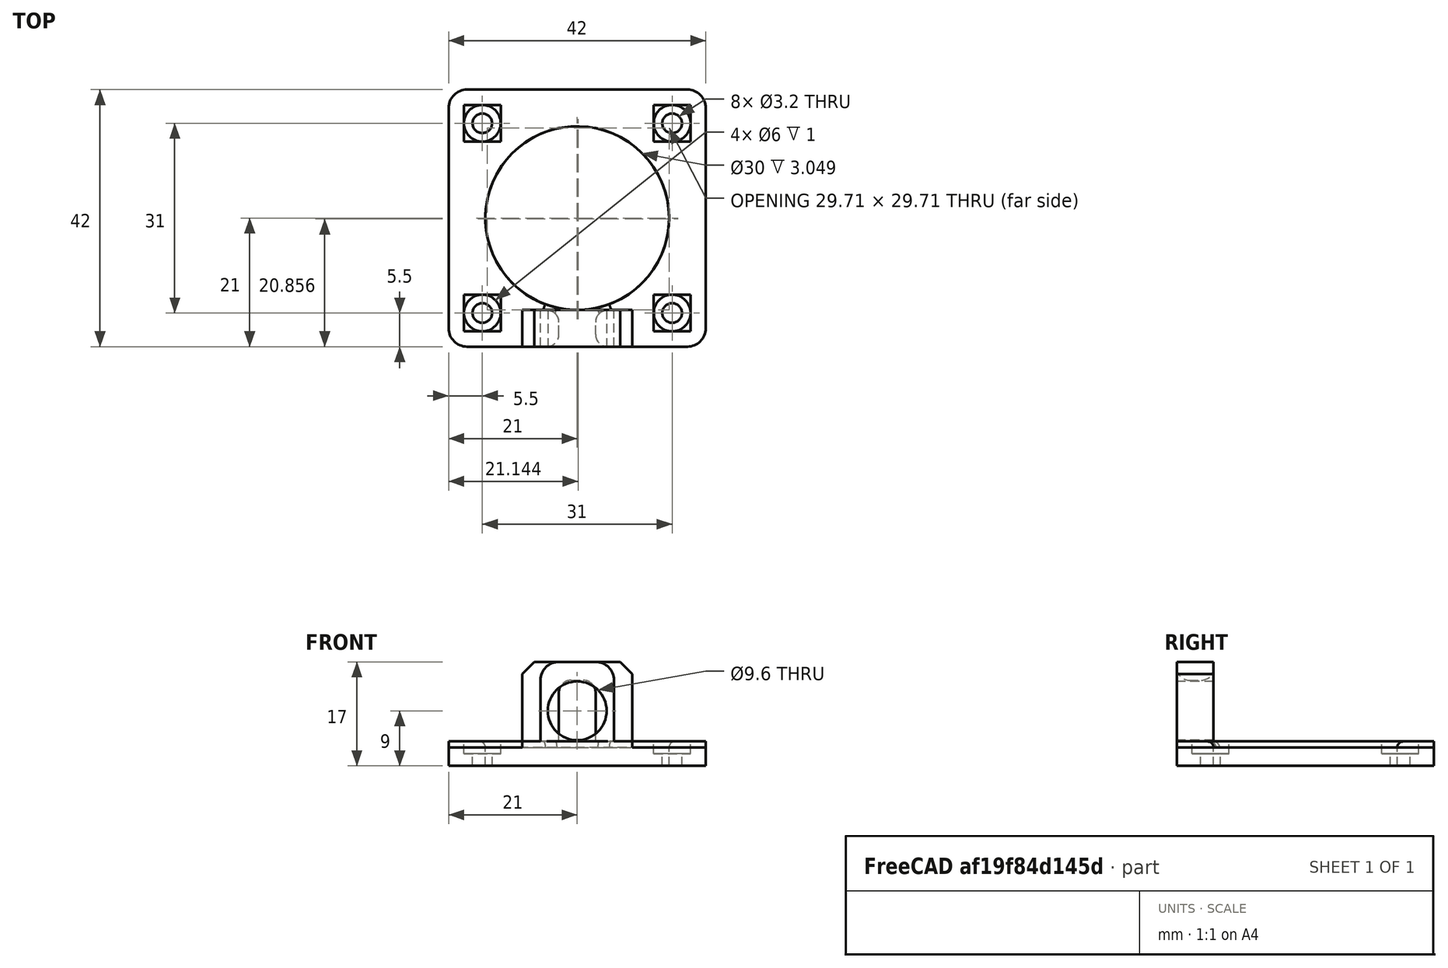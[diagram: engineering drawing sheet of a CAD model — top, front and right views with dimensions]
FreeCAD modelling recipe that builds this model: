
FCSTD DOCUMENT  (FreeCAD 0.18R14555 (Git shallow))
Label: tube-mounter
License: All rights reserved
LicenseURL: http://en.wikipedia.org/wiki/All_rights_reserved
objects: Part::Cylinder×15, Part::Box×9, Part::Cut×8, Part::MultiFuse×6, Part::Fillet×5, Part::Chamfer×1
note: 44 computed .brp shape members not serialized (recipe doc carries the construction recipe); baked Part::Feature solids carry a one-line shape summary decoded from their .brp

FEATURE [Part::Box] Box  label="Cube"
  AttacherType = Attacher::AttachEngine3D
  Height = 3
  Length = 42
  Width = 42
FEATURE [Part::Cylinder] Cylinder
  Angle = 360
  AttacherType = Attacher::AttachEngine3D
  Height = 3
  Placement = pos=(5.5,5.5,0) rot=(0,0,1;0rad)
  Radius = 1.6
FEATURE [Part::Cylinder] Cylinder001
  Angle = 360
  AttacherType = Attacher::AttachEngine3D
  Height = 3
  Placement = pos=(36.5,5.5,0) rot=(0,0,1;0rad)
  Radius = 1.6
FEATURE [Part::Cylinder] Cylinder002
  Angle = 360
  AttacherType = Attacher::AttachEngine3D
  Height = 3
  Placement = pos=(5.5,36.5,0) rot=(0,0,1;0rad)
  Radius = 1.6
FEATURE [Part::Cylinder] Cylinder003
  Angle = 360
  AttacherType = Attacher::AttachEngine3D
  Height = 3
  Placement = pos=(36.5,36.5,0) rot=(0,0,1;0rad)
  Radius = 1.6
FEATURE [Part::Box] Box001  label="Cube001"
  AttacherType = Attacher::AttachEngine3D
  Height = 2
  Length = 6
  Placement = pos=(2.5,2.5,1) rot=(0,0,1;0rad)
  Width = 6
FEATURE [Part::Cylinder] Cylinder004
  Angle = 360
  AttacherType = Attacher::AttachEngine3D
  Height = 1
  Placement = pos=(36.5,36.5,0) rot=(0,0,1;0rad)
  Radius = 3
FEATURE [Part::Cylinder] Cylinder005
  Angle = 360
  AttacherType = Attacher::AttachEngine3D
  Height = 1
  Placement = pos=(5.5,5.5,0) rot=(0,0,1;0rad)
  Radius = 3
FEATURE [Part::Cylinder] Cylinder006
  Angle = 360
  AttacherType = Attacher::AttachEngine3D
  Height = 1
  Placement = pos=(36.5,5.5,0) rot=(0,0,1;0rad)
  Radius = 3
FEATURE [Part::Cylinder] Cylinder007
  Angle = 360
  AttacherType = Attacher::AttachEngine3D
  Height = 1
  Placement = pos=(5.5,36.5,0) rot=(0,0,1;0rad)
  Radius = 3
FEATURE [Part::MultiFuse] Fusion
  Shapes = -> [Cylinder003,Cylinder,Cylinder001,Cylinder002]
FEATURE [Part::MultiFuse] Fusion001
  Placement = pos=(0,0,2) rot=(0,0,1;0rad)
  Shapes = -> [Cylinder004,Cylinder007,Cylinder006,Cylinder005]
FEATURE [Part::Box] Box002  label="Cube002"
  AttacherType = Attacher::AttachEngine3D
  Height = 4
  Length = 42
  Width = 42
FEATURE [Part::Cut] Cut
  Base = -> Box
  Tool = -> Fusion
FEATURE [Part::Cut] Cut001
  Base = -> Cut
  Tool = -> Fusion001
FEATURE [Part::Fillet] Fillet
  Base = -> Cut001
  Edges = 4 edges r=3: [Edge1,Edge3,Edge6,Edge15]
FEATURE [Part::Cylinder] Cylinder008
  Angle = 360
  AttacherType = Attacher::AttachEngine3D
  Height = 3
  Placement = pos=(21,21,0) rot=(0,0,1;0rad)
  Radius = 15
FEATURE [Part::Cut] Cut002
  Base = -> Fillet
  Tool = -> Cylinder008
FEATURE [Part::Box] Box003  label="Cube003"
  AttacherType = Attacher::AttachEngine3D
  Height = 2
  Length = 6
  Placement = pos=(33.5,2.5,1) rot=(0,0,1;0rad)
  Width = 6
FEATURE [Part::Box] Box004  label="Cube004"
  AttacherType = Attacher::AttachEngine3D
  Height = 2
  Length = 6
  Placement = pos=(2.5,33.5,1) rot=(0,0,1;0rad)
  Width = 6
FEATURE [Part::Box] Box005  label="Cube005"
  AttacherType = Attacher::AttachEngine3D
  Height = 2
  Length = 6
  Placement = pos=(33.5,33.5,1) rot=(0,0,1;0rad)
  Width = 6
FEATURE [Part::MultiFuse] Fusion002
  Placement = pos=(0,0,1) rot=(0,0,1;0rad)
  Shapes = -> [Box003,Box004,Box005,Box001]
FEATURE [Part::Cut] Cut003
  Base = -> Box002
  Tool = -> Fusion002
FEATURE [Part::Cylinder] Cylinder009
  Angle = 360
  AttacherType = Attacher::AttachEngine3D
  Height = 4
  Placement = pos=(5.5,5.5,0) rot=(0,0,1;0rad)
  Radius = 1.6
FEATURE [Part::Cylinder] Cylinder010
  Angle = 360
  AttacherType = Attacher::AttachEngine3D
  Height = 4
  Placement = pos=(36.5,5.5,0) rot=(0,0,1;0rad)
  Radius = 1.6
FEATURE [Part::Cylinder] Cylinder011
  Angle = 360
  AttacherType = Attacher::AttachEngine3D
  Height = 4
  Placement = pos=(5.5,36.5,0) rot=(0,0,1;0rad)
  Radius = 1.6
FEATURE [Part::Cylinder] Cylinder012
  Angle = 360
  AttacherType = Attacher::AttachEngine3D
  Height = 4
  Placement = pos=(36.5,36.5,0) rot=(0,0,1;0rad)
  Radius = 1.6
FEATURE [Part::MultiFuse] Fusion003
  Shapes = -> [Cylinder009,Cylinder010,Cylinder011,Cylinder012]
FEATURE [Part::Cut] Cut004
  Base = -> Cut003
  Tool = -> Fusion003
FEATURE [Part::Fillet] Fillet001
  Base = -> Cut004
  Edges = 4 edges r=3: [Edge1,Edge3,Edge6,Edge27]
FEATURE [Part::Cylinder] Cylinder013
  Angle = 360
  AttacherType = Attacher::AttachEngine3D
  Height = 10
  Placement = pos=(21,21,0) rot=(0,0,1;0rad)
  Radius = 15
FEATURE [Part::Cut] Cut005  label="bottom"
  Base = -> Fillet001
  Tool = -> Cylinder013
FEATURE [Part::Box] Box006  label="Cube006"
  AttacherType = Attacher::AttachEngine3D
  Height = 17
  Length = 18
  Placement = pos=(12,0,0) rot=(0,0,1;0rad)
  Width = 6
FEATURE [Part::Cylinder] Cylinder014
  Angle = 360
  AttacherType = Attacher::AttachEngine3D
  Height = 6
  Placement = pos=(21,6,9) rot=(1,0,0;1.5708rad)
  Radius = 4.8
FEATURE [Part::Box] Box007  label="Cube007"
  AttacherType = Attacher::AttachEngine3D
  Height = 17
  Length = 12
  Width = 6
FEATURE [Part::Box] Box008  label="Cube008"
  AttacherType = Attacher::AttachEngine3D
  Height = 14
  Length = 6
  Placement = pos=(3,0,0) rot=(0,0,1;0rad)
  Width = 6
FEATURE [Part::Cut] Cut007
  Base = -> Box007
  Placement = pos=(15,0,0) rot=(0,0,1;0rad)
  Tool = -> Box008
FEATURE [Part::Fillet] Fillet002
  Base = -> Cut007
  Edges = 2 edges r=3: [Edge2,Edge13]
FEATURE [Part::Fillet] Fillet003
  Base = -> Fillet002
  Edges = 8 edges r=2: [Edge9,Edge11,Edge12,Edge22,Edge23,Edge24,Edge29,Edge30]
FEATURE [Part::MultiFuse] Fusion005
  Shapes = -> [Cut005,Fillet003]
FEATURE [Part::Fillet] Fillet004
  Base = -> Fusion005
  Edges = 1 edges r=1: [Edge36]
FEATURE [Part::Cut] Cut008
  Base = -> Box006
  Tool = -> Cylinder014
FEATURE [Part::Chamfer] Chamfer
  Base = -> Cut008
  Edges = 2 edges r=2: [Edge2,Edge10]
FEATURE [Part::MultiFuse] Fusion006
  Shapes = -> [Chamfer,Cut002]
